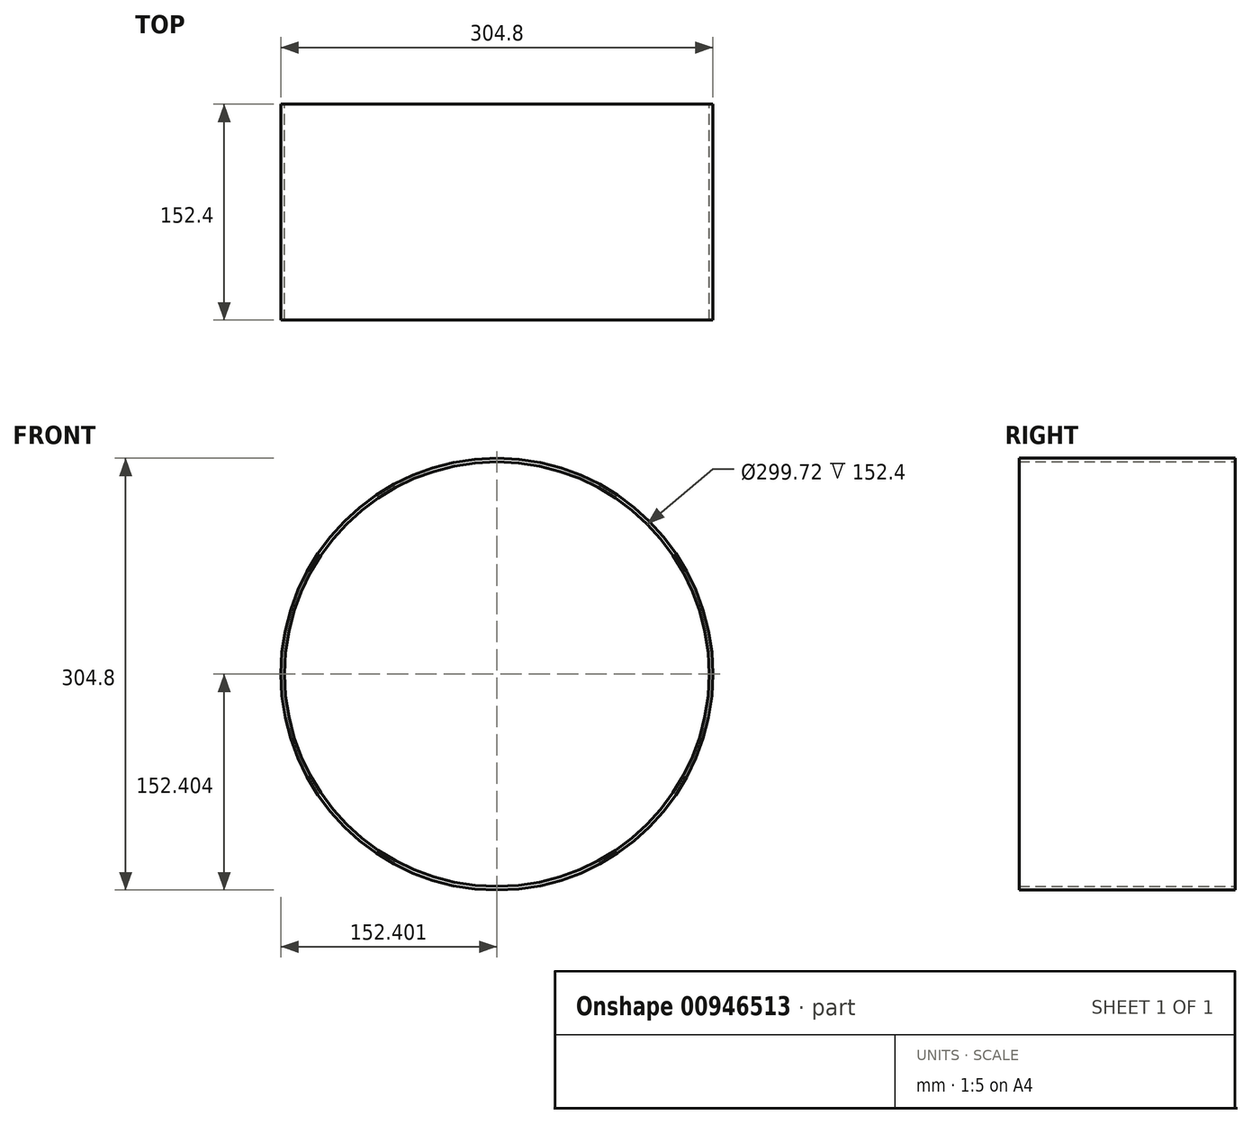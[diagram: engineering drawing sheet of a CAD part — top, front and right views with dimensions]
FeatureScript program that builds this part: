
annotation { "Feature Type Name" : "Feature", "Feature Type Description" : "" }
export const myFeature = defineFeature(function(context is Context, id is Id, definition is map)
    precondition{}
    {
        {
            var Q0;
            Q0=qCreatedBy(makeId("Front.planeOp"),FACE);
            var sketch = newSketch(context, id + "F0", { "sketchPlane" : qUnion([Q0])});
            skCircle(sketch, "E0", {"center": v(-115, 10) * mm, "radius": 152.4 * mm});
            skCircle(sketch, "E1", {"center": v(-115, 10) * mm, "radius": 149.86 * mm});
            skSolve(sketch);
        }
        {
            var Q0;
            Q0 = qSketchRegion(id + "F0", true);
            extrude(context, id + "F1", {"entities" : qUnion([Q0]), "depth" : 152.4 * mm, "offsetDistance" : 25.4 * mm});
        }
    });
